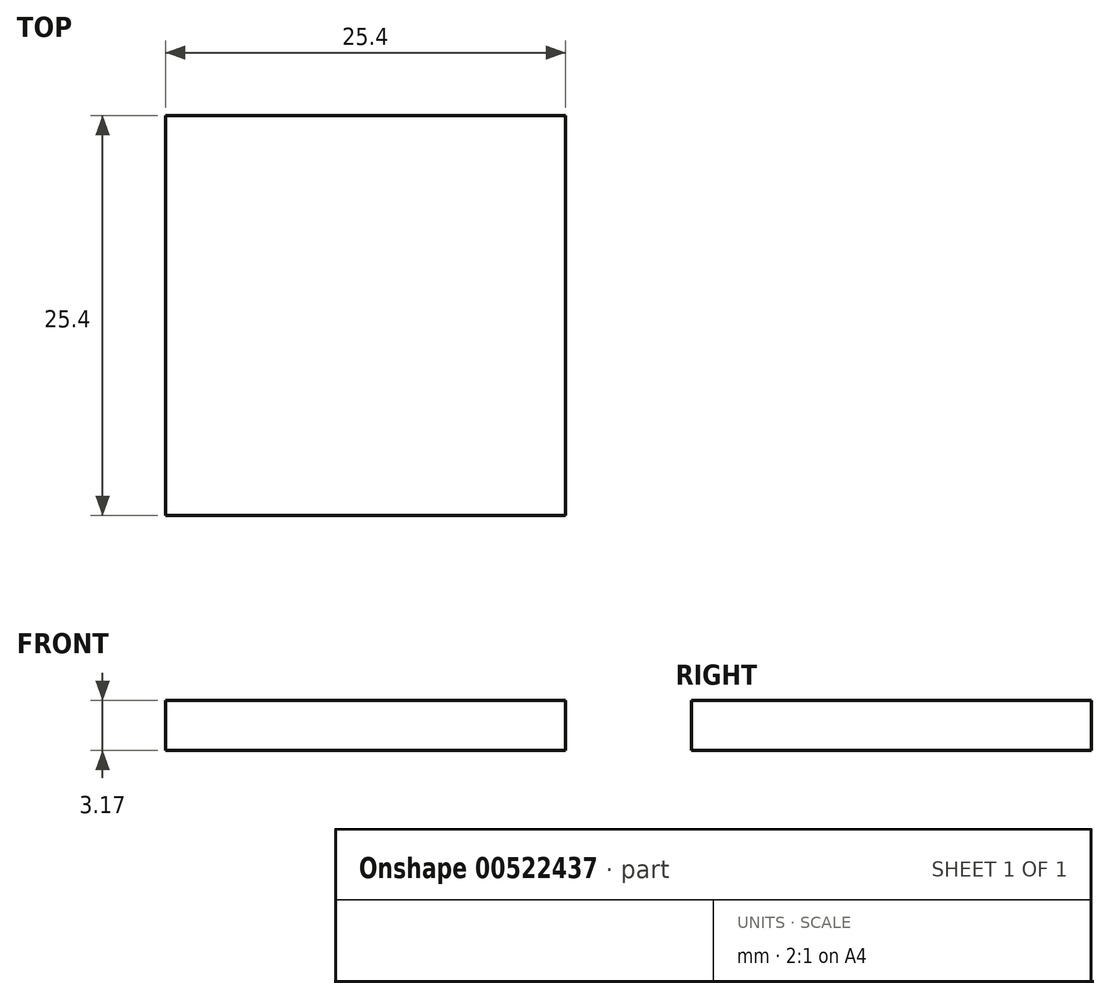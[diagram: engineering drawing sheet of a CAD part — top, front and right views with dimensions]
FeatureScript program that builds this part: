
annotation { "Feature Type Name" : "Feature", "Feature Type Description" : "" }
export const myFeature = defineFeature(function(context is Context, id is Id, definition is map)
    precondition{}
    {
        {
            var Q0;
            Q0=qCreatedBy(makeId("Top.planeOp"),FACE);
            var sketch = newSketch(context, id + "F0", { "sketchPlane" : qUnion([Q0])});
            skLineSegment(sketch, "E0.bottom", {"start": v(-25.4, 11.4) * mm, "end": v(0, 11.4) * mm});
            skLineSegment(sketch, "E0.top", {"start": v(-25.4, -14) * mm, "end": v(0, -14) * mm});
            skLineSegment(sketch, "E0.left", {"start": v(-25.4, 11.4) * mm, "end": v(-25.4, -14) * mm});
            skLineSegment(sketch, "E0.right", {"start": v(0, 11.4) * mm, "end": v(0, -14) * mm});
            skSolve(sketch);
        }
        {
            var Q0;
            Q0 = qSketchRegion(id + "F0", true);
            extrude(context, id + "F1", {"entities" : qUnion([Q0]), "depth" : 3.17 * mm, "offsetDistance" : 25.4 * mm});
        }
    });
